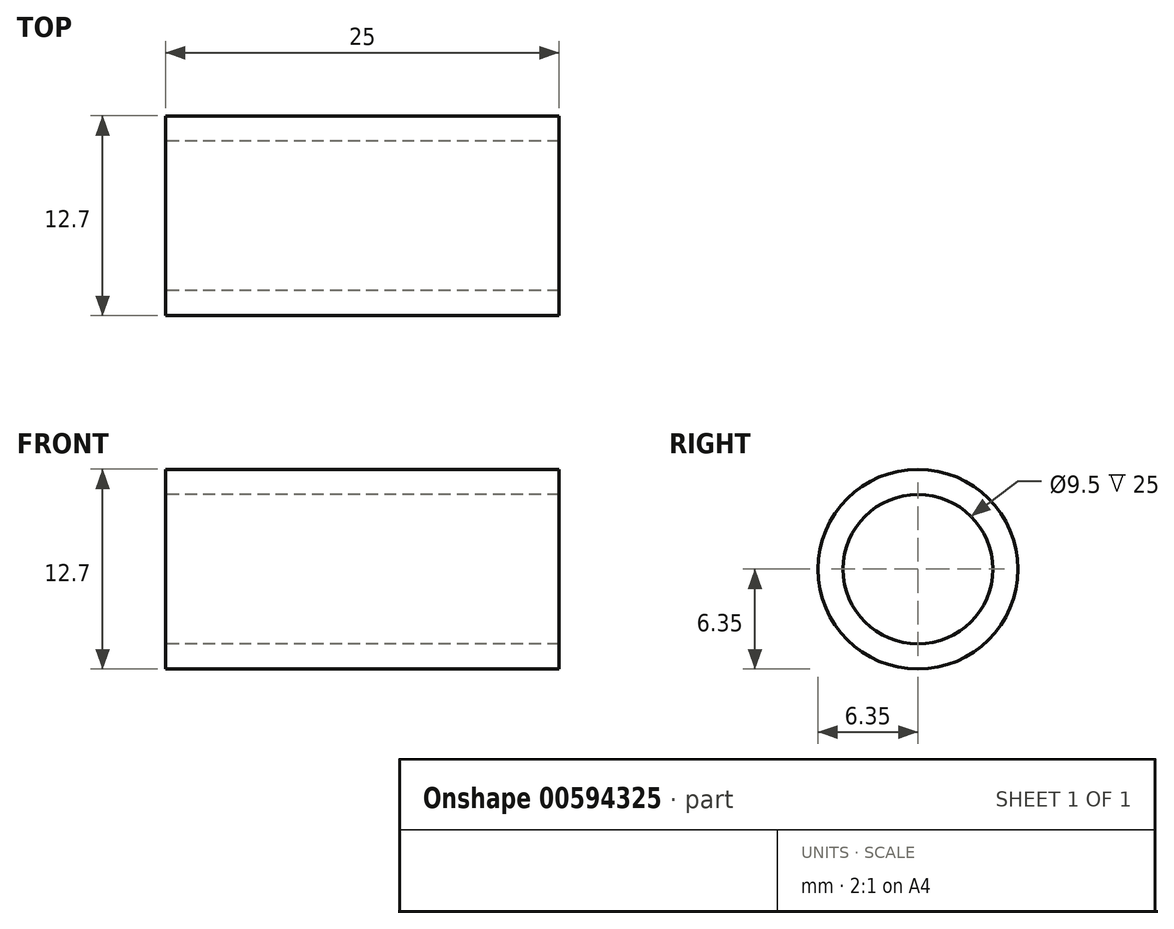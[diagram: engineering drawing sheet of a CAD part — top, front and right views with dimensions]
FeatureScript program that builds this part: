
annotation { "Feature Type Name" : "Feature", "Feature Type Description" : "" }
export const myFeature = defineFeature(function(context is Context, id is Id, definition is map)
    precondition{}
    {
        {
            var Q0;
            Q0=qCreatedBy(makeId("Right.planeOp"),FACE);
            var sketch = newSketch(context, id + "F0", { "sketchPlane" : qUnion([Q0])});
            skCircle(sketch, "E0", {"center": v(0, 0) * mm, "radius": 4.75 * mm});
            skCircle(sketch, "E1", {"center": v(0, 0) * mm, "radius": 6.35 * mm});
            skSolve(sketch);
        }
        {
            var Q0;
            Q0=makeQuery(id+"F0.imprint","IMPRINT",FACE,{"disambiguationData":[TD([[makeQuery(id+"F0.imprint","IMPRINT",EDGE,{"derivedFrom":sQuery(id+"F0.wireOp",EDGE,"E0")}),-1.0]])]});
            extrude(context, id + "F1", {"entities" : qUnion([Q0]), "depth" : 25 * mm, "offsetDistance" : 25 * mm});
        }
    });
